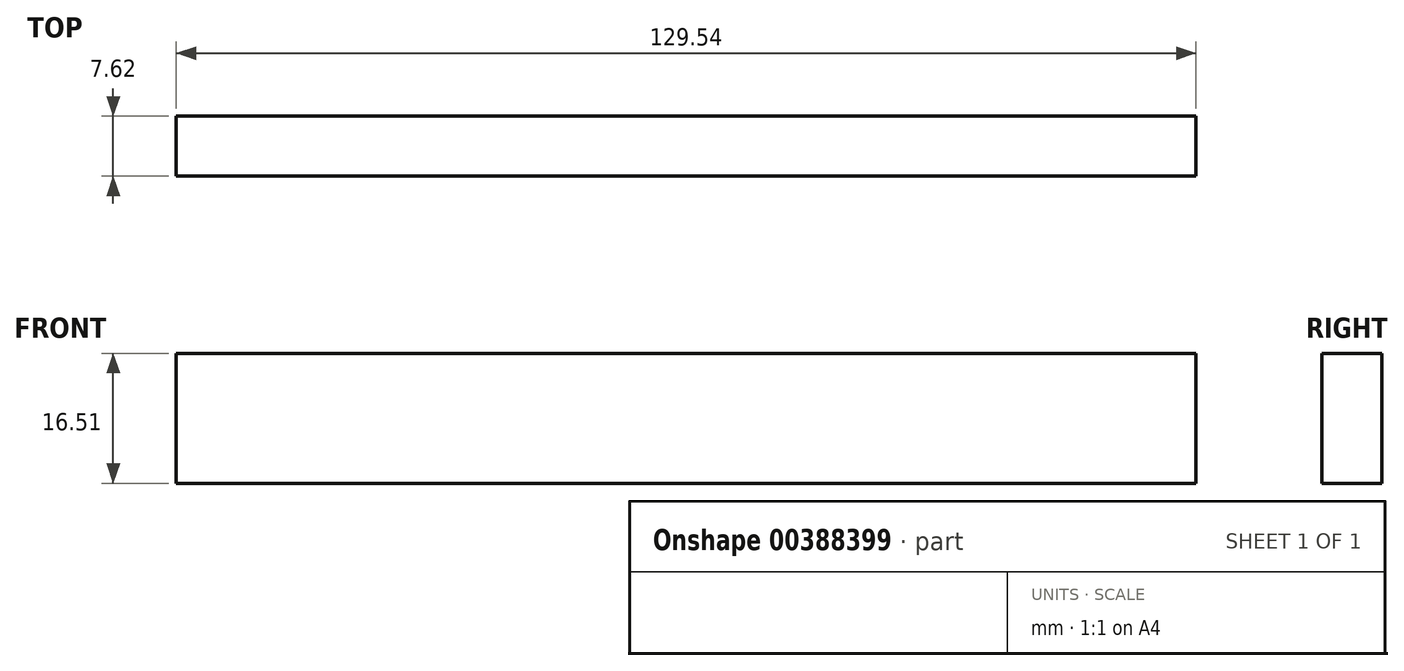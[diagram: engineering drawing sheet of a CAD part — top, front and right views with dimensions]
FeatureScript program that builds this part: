
annotation { "Feature Type Name" : "Feature", "Feature Type Description" : "" }
export const myFeature = defineFeature(function(context is Context, id is Id, definition is map)
    precondition{}
    {
        {
            var Q0;
            Q0=qCreatedBy(makeId("Front.planeOp"),FACE);
            var sketch = newSketch(context, id + "F0", { "sketchPlane" : qUnion([Q0])});
            skLineSegment(sketch, "E0.bottom", {"start": v(0, 0) * mm, "end": v(129.54, 0) * mm});
            skLineSegment(sketch, "E0.top", {"start": v(0, -16.51) * mm, "end": v(129.54, -16.51) * mm});
            skLineSegment(sketch, "E0.left", {"start": v(0, 0) * mm, "end": v(0, -16.51) * mm});
            skLineSegment(sketch, "E0.right", {"start": v(129.54, 0) * mm, "end": v(129.54, -16.51) * mm});
            skSolve(sketch);
        }
        {
            var Q0;
            Q0 = qSketchRegion(id + "F0", true);
            extrude(context, id + "F1", {"entities" : qUnion([Q0]), "depth" : 7.62 * mm});
        }
    });
